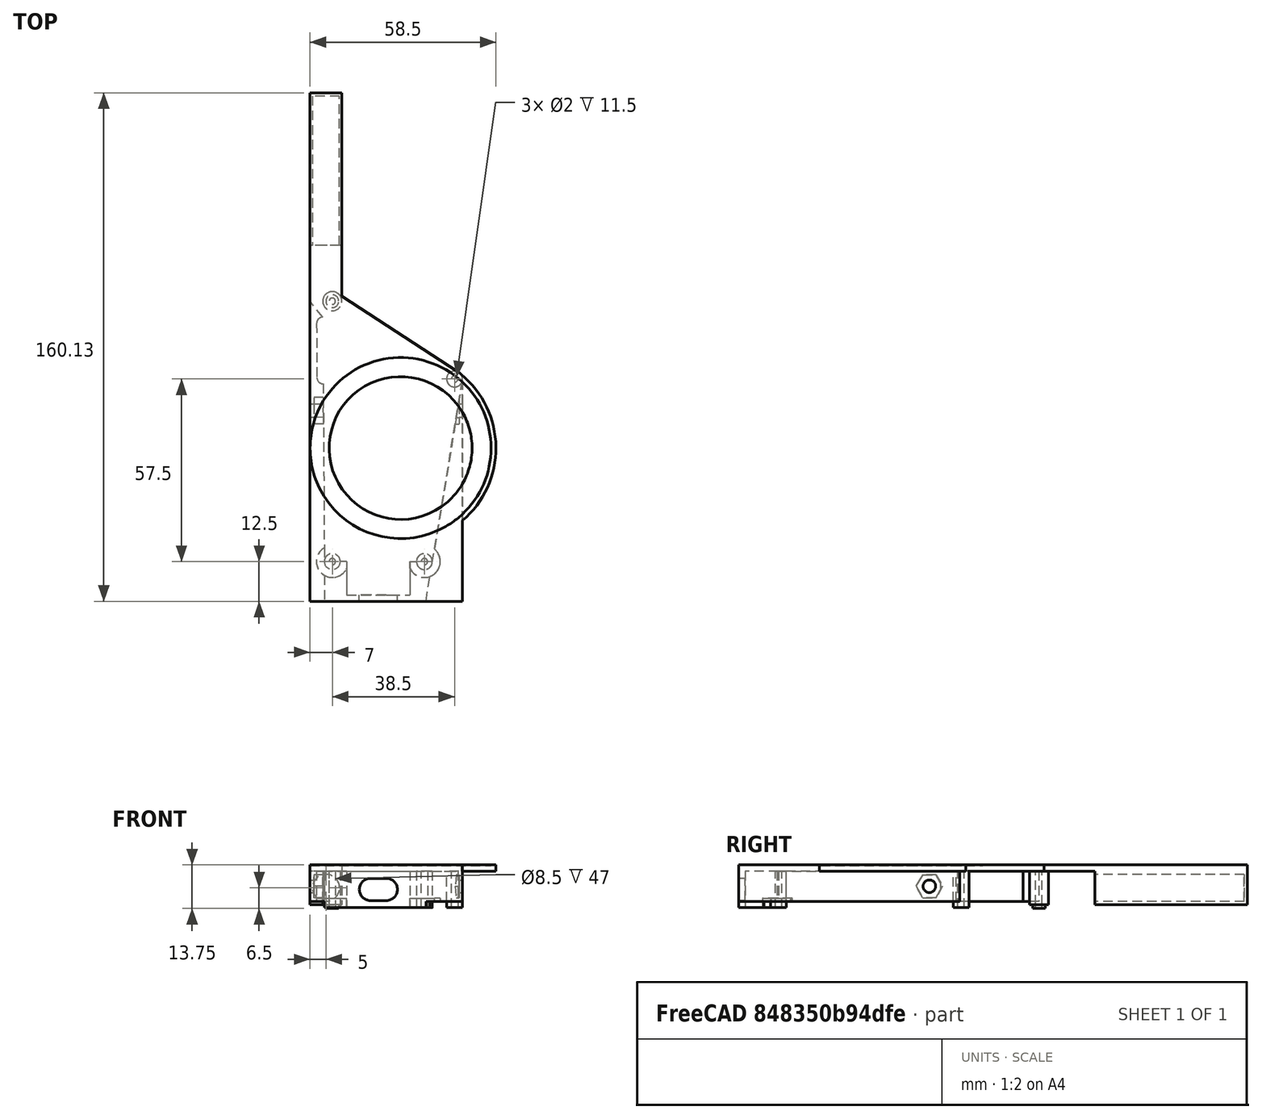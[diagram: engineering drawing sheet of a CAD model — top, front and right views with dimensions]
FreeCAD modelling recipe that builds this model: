
FCSTD DOCUMENT  (FreeCAD 0.19R24276 (Git))
Label: dims_test
License: All rights reserved
LicenseURL: http://en.wikipedia.org/wiki/All_rights_reserved
objects: Sketcher::SketchObject×17, PartDesign::Pad×9, PartDesign::Pocket×8, Spreadsheet::Sheet×2, PartDesign::Plane×1, PartDesign::Body×1, Part::Mirroring×1
note: 54 computed .brp shape members not serialized (recipe doc carries the construction recipe); baked Part::Feature solids carry a one-line shape summary decoded from their .brp

FEATURE [Spreadsheet::Sheet] Spreadsheet  label="dims"
  cells = A1=bottom screw gap; B1(bottom_screw_gap)=29; A2=bottom to antenna; B2(bottom_to_antenna_gap)=82; A3=standoff height; B3(standoff_height)=11.5; A4=standoff diam; B4(standoff_diam)=5; A5=antenna snugger diam; B5(antenna_snugger_diam)=4; A6=antenna snugger height; B6(antenna_snugger_height)=1.25; A7=standoff screw diam; B7(screw_diam)=2; A8=antenna standoff width; B8(antenna_standoff_diam)=6; A9=antenna standoff height; B9(antenna_standoff_height)==standoff_height - 1; A10=side mount offset height; B10(side_mount_offset_height)=57.5; A11=side mount offset width; B11(side_mount_offset_width)=9.5; A13=antenna diam; B13(antenna_diam)=8.5; A15=ring outer diam; B15(ring_outer_diam)==57mm; A16=ring inner diam; B16(ring_inner_diam)==45mm; A17=ring thickness; B17(ring_thickness)==0.25mm
FEATURE [Sketcher::SketchObject] Sketch
  FullyConstrained = true
  MapMode = 5
  Support = -> [XY_Plane]
  expr: Constraints[13] = <<dims>>.bottom_screw_gap
  expr: Constraints[12] = <<dims>>.standoff_diam
  expr: Constraints[3] = <<dims>>.screw_diam
  expr: Constraints[4] = <<dims>>.bottom_to_antenna_gap
  expr: Constraints[25] = <<dims>>.antenna_standoff_diam
  expr: Constraints[18] = <<dims>>.side_mount_offset_width
  expr: Constraints[17] = <<dims>>.side_mount_offset_height
  expr: Constraints[47] = <<otg_adapter_dims>>.stickout
  sketch-geometry (18):
    g0: Circle CenterX=0 CenterY=0 CenterZ=0 NormalX=0 NormalY=0 NormalZ=1 AngleXU=0 Radius=1
    g1: Circle CenterX=0 CenterY=82 CenterZ=0 NormalX=0 NormalY=0 NormalZ=1 AngleXU=0 Radius=1
    g2: Circle CenterX=0 CenterY=82 CenterZ=0 NormalX=0 NormalY=0 NormalZ=1 AngleXU=0 Radius=2.5
    g3: Circle CenterX=0 CenterY=0 CenterZ=0 NormalX=0 NormalY=0 NormalZ=1 AngleXU=0 Radius=2.5
    g4: Circle CenterX=29 CenterY=0 CenterZ=0 NormalX=0 NormalY=0 NormalZ=1 AngleXU=0 Radius=2.5
    g5: Circle CenterX=29 CenterY=0 CenterZ=0 NormalX=0 NormalY=0 NormalZ=1 AngleXU=0 Radius=2.5
    g6: Circle CenterX=38.5 CenterY=57.5 CenterZ=0 NormalX=0 NormalY=0 NormalZ=1 AngleXU=0 Radius=2.5
    g7: Circle CenterX=38.5 CenterY=57.5 CenterZ=0 NormalX=0 NormalY=0 NormalZ=1 AngleXU=0 Radius=1
    g8: Circle CenterX=29 CenterY=0 CenterZ=0 NormalX=0 NormalY=0 NormalZ=1 AngleXU=0 Radius=1
    g9: LineSegment StartX=1.63826 StartY=84.5132 StartZ=0 EndX=39.8652 EndY=59.5943 EndZ=0
    g10: LineSegment StartX=31.4666 StartY=-0.4075 StartZ=0 EndX=40.9666 EndY=57.0925 EndZ=0
    g11: Circle CenterX=0 CenterY=82 CenterZ=0 NormalX=0 NormalY=0 NormalZ=1 AngleXU=0 Radius=3
    g12: ArcOfCircle CenterX=0 CenterY=82 CenterZ=0 NormalX=0 NormalY=0 NormalZ=1 AngleXU=0 Radius=3 StartAngle=0.99311 EndAngle=3.14769
    g13: ArcOfCircle CenterX=38.5 CenterY=57.5 CenterZ=0 NormalX=0 NormalY=0 NormalZ=1 AngleXU=0 Radius=2.5 StartAngle=6.11945 EndAngle=7.27629
    g14: LineSegment StartX=31.4666 StartY=-0.4075 StartZ=0 EndX=29.4687 EndY=-12.5 EndZ=0
    g15: LineSegment StartX=-2.42383 StartY=-12.5 StartZ=0 EndX=29.4687 EndY=-12.5 EndZ=0
    g16: LineSegment StartX=-2.99994 StartY=81.9817 StartZ=0 EndX=-2.42383 EndY=-12.5 EndZ=0
    g17: LineSegment StartX=-2.4848 StartY=-2.5 StartZ=0 EndX=31.1208 EndY=-2.5 EndZ=0
  constraints (48):
    c: Coincident(g0,g-1)
    c: PointOnObject(g1,g-2)
    c: Equal(g1,g0)
    c: Diameter(g1) = 2
    c: Distance(g1,g0) = 82
    c: Coincident(g2,g1)
    c: Coincident(g3,g0)
    c: PointOnObject(g4,g-1)
    c: Equal(g3,g4)
    c: Coincident(g5,g4)
    c: Equal(g3,g5)
    c: Equal(g5,g2)
    c: Diameter(g2) = 5
    c: Distance(g4,g0) = 29
    c: Coincident(g7,g6)
    c: Equal(g1,g7)
    c: Equal(g6,g2)
    c: DistanceY(g4,g6) = 57.5
    c: DistanceX(g4,g6) = 9.5
    c: Coincident(g8,g4)
    c: Equal(g0,g8)
    c: Tangent(g9,g6)
    c: Tangent(g10,g4)
    c: Tangent(g10,g6)
    c: Coincident(g11,g1)
    c: Diameter(g11) = 6
    c: Tangent(g9,g11)
    c: PointOnObject(g9,g11)
    c: Coincident(g12,g1)
    c: Coincident(g12,g9)
    c: Coincident(g9,g13)
    c: Coincident(g10,g13)
    c: PointOnObject(g10,g6)
    c: PointOnObject(g10,g4)
    c: Coincident(g13,g6)
    c: Coincident(g14,g10)
    c: Coincident(g15,g14)
    c: Horizontal(g15)
    c: Parallel(g14,g10)
    c: Coincident(g16,g12)
    c: Coincident(g16,g15)
    c: Tangent(g16,g3)
    c: Tangent(g16,g11)
    c: PointOnObject(g17,g16)
    c: PointOnObject(g17,g14)
    c: Horizontal(g17)
    c: Tangent(g17,g4)
    c: DistanceY(g14,g17) = 10
FEATURE [PartDesign::Pad] Pad  label="base plate"
  Direction = (1,1,1)
  Length = 2
  Length2 = 100
  Profile = -> Sketch
  Type = 0
FEATURE [Sketcher::SketchObject] Sketch001
  ExternalGeometry = -> [Pad]
  FullyConstrained = true
  MapMode = 5
  Placement = pos=(0,0,2) rot=(0,0,1;0rad)
  Support = -> [Pad]
  expr: Constraints[4] = <<dims>>.screw_diam
  expr: Constraints[10] = <<dims>>.bottom_screw_gap
  expr: Constraints[12] = <<dims>>.standoff_diam
  sketch-geometry (6):
    g0: Circle CenterX=0 CenterY=0 CenterZ=0 NormalX=0 NormalY=0 NormalZ=1 AngleXU=0 Radius=2.5
    g1: Circle CenterX=29 CenterY=0 CenterZ=0 NormalX=0 NormalY=0 NormalZ=1 AngleXU=0 Radius=2.5
    g2: Circle CenterX=29 CenterY=0 CenterZ=0 NormalX=0 NormalY=0 NormalZ=1 AngleXU=0 Radius=1
    g3: Circle CenterX=0 CenterY=0 CenterZ=0 NormalX=0 NormalY=0 NormalZ=1 AngleXU=0 Radius=1
    g4: Circle CenterX=38.5 CenterY=57.5 CenterZ=0 NormalX=0 NormalY=0 NormalZ=1 AngleXU=0 Radius=2.5
    g5: Circle CenterX=38.5 CenterY=57.5 CenterZ=0 NormalX=0 NormalY=0 NormalZ=1 AngleXU=0 Radius=1
  constraints (13):
    c: Coincident(g0,g-1)
    c: Coincident(g2,g1)
    c: Coincident(g3,g0)
    c: Equal(g2,g3)
    c: Diameter(g3) = 2
    c: Equal(g0,g1)
    c: Coincident(g4,g-4)
    c: Coincident(g5,g4)
    c: Equal(g3,g5)
    c: PointOnObject(g1,g-1)
    c: DistanceX(g0,g1) = 29
    c: Equal(g4,g1)
    c: Diameter(g1) = 5
FEATURE [PartDesign::Pad] Pad003  label="standoffs"
  BaseFeature = -> Pad
  Direction = (1,1,1)
  Length = 11.5
  Length2 = 100
  Profile = -> Sketch001
  Type = 0
  expr: Length = <<dims>>.standoff_height
FEATURE [Sketcher::SketchObject] Sketch003
  ExternalGeometry = -> [Pad003]
  FullyConstrained = true
  MapMode = 5
  Placement = pos=(0,0,2) rot=(0,0,1;0rad)
  Support = -> [Pad003]
  expr: Constraints[3] = <<dims>>.screw_diam
  sketch-geometry (2):
    g0: Circle CenterX=0 CenterY=82 CenterZ=0 NormalX=0 NormalY=0 NormalZ=1 AngleXU=0 Radius=3
    g1: Circle CenterX=0 CenterY=82 CenterZ=0 NormalX=0 NormalY=0 NormalZ=1 AngleXU=0 Radius=1
  constraints (4):
    c: Coincident(g0,g-3)
    c: PointOnObject(g-3,g0)
    c: Coincident(g1,g0)
    c: Diameter(g1) = 2
FEATURE [PartDesign::Pad] Pad004  label="antenna standoff"
  BaseFeature = -> Pad003
  Direction = (1,1,1)
  Length = 10.5
  Length2 = 100
  Profile = -> Sketch003
  Type = 0
  expr: Length = <<dims>>.antenna_standoff_height
FEATURE [Sketcher::SketchObject] Sketch006
  ExternalGeometry = -> [Pad004]
  FullyConstrained = true
  MapMode = 5
  Placement = pos=(0,0,12.5) rot=(0,0,1;0rad)
  Support = -> [Pad004]
  expr: Constraints[3] = <<dims>>.antenna_snugger_diam
  sketch-geometry (2):
    g0: Circle CenterX=0 CenterY=82 CenterZ=0 NormalX=0 NormalY=0 NormalZ=1 AngleXU=0 Radius=2
    g1: Circle CenterX=0 CenterY=82 CenterZ=0 NormalX=0 NormalY=0 NormalZ=1 AngleXU=0 Radius=1
  constraints (4):
    c: Coincident(g0,g-3)
    c: Coincident(g1,g0)
    c: Equal(g1,g-3)
    c: Diameter(g0) = 4
FEATURE [PartDesign::Pad] Pad007  label="antenna snugger"
  BaseFeature = -> Pad004
  Direction = (1,1,1)
  Length = 1.25
  Length2 = 100
  Profile = -> Sketch006
  Type = 0
  expr: Length = <<dims>>.antenna_snugger_height
FEATURE [Spreadsheet::Sheet] Spreadsheet001  label="otg_adapter_dims"
  cells = A1=width; B1(width)=20; A2=length; B2(length)=32; A3=lightning width; B3(lightning_width)=12; A4=lightning height; B4(lightning_height)=7; A5=stickout; B5(stickout)=10
FEATURE [Sketcher::SketchObject] Sketch011
  ExternalGeometry = -> [Pad007]
  FullyConstrained = true
  MapMode = 5
  Support = -> [XY_Plane]
  sketch-geometry (8):
    g0: LineSegment StartX=-7 StartY=147.626 StartZ=0 EndX=3 EndY=147.626 EndZ=0
    g1: LineSegment StartX=3 StartY=147.626 StartZ=0 EndX=3 EndY=83.6255 EndZ=0
    g2: LineSegment StartX=-7 StartY=147.626 StartZ=0 EndX=-7 EndY=82 EndZ=0
    g3: LineSegment StartX=-7 StartY=82 StartZ=0 EndX=-2.96946 EndY=76.9817 EndZ=0
    g4: LineSegment StartX=1.63826 StartY=84.5132 StartZ=0 EndX=3 EndY=83.6255 EndZ=0
    g5: ArcOfCircle CenterX=0 CenterY=82 CenterZ=0 NormalX=0 NormalY=0 NormalZ=1 AngleXU=0 Radius=3 StartAngle=0.99311 EndAngle=3.14769
    g6: LineSegment StartX=-7 StartY=82 StartZ=0 EndX=3 EndY=82 EndZ=0
    g7: LineSegment StartX=-2.99994 StartY=81.9817 StartZ=0 EndX=-2.96946 EndY=76.9817 EndZ=0
  constraints (23):
    c: Horizontal(g0)
    c: Coincident(g1,g0)
    c: PointOnObject(g1,g-3)
    c: Vertical(g1)
    c: Coincident(g2,g0)
    c: Vertical(g2)
    c: Coincident(g3,g2)
    c: PointOnObject(g3,g-5)
    c: Coincident(g4,g-3)
    c: Coincident(g4,g1)
    c: Coincident(g5,g-4)
    c: Coincident(g5,g4)
    c: PointOnObject(g5,g-5)
    c: DistanceY(g3,g5) = 5
    c: Coincident(g6,g2)
    c: PointOnObject(g6,g-4)
    c: Horizontal(g6)
    c: PointOnObject(g5,g6)
    c: Distance(g0) = 10
    c: Tangent(g1,g-4)
    c: Coincident(g7,g5)
    c: Coincident(g7,g3)
    c: Distance(g1) = 64
FEATURE [PartDesign::Pad] Pad010  label="antenna cover base"
  BaseFeature = -> Pad007
  Direction = (1,1,1)
  Length = 10
  Length2 = 100
  Profile = -> Sketch011
  Type = 3
  UpToFace = -> Pad007 [Face7]
FEATURE [Sketcher::SketchObject] Sketch008
  ExternalGeometry = -> [Pad010]
  FullyConstrained = true
  MapMode = 5
  Placement = pos=(0,0,2) rot=(0,0,1;0rad)
  Support = -> [Pad010]
  sketch-geometry (4):
    g0: LineSegment StartX=-7 StartY=147.626 StartZ=0 EndX=3 EndY=147.626 EndZ=0
    g1: LineSegment StartX=3 StartY=147.626 StartZ=0 EndX=3 EndY=99.6255 EndZ=0
    g2: LineSegment StartX=3 StartY=99.6255 StartZ=0 EndX=-7 EndY=99.6255 EndZ=0
    g3: LineSegment StartX=-7 StartY=99.6255 StartZ=0 EndX=-7 EndY=147.626 EndZ=0
  constraints (11):
    c: Coincident(g0,g1)
    c: Coincident(g1,g2)
    c: Coincident(g2,g3)
    c: Coincident(g3,g0)
    c: Horizontal(g0)
    c: Horizontal(g2)
    c: Vertical(g1)
    c: Vertical(g3)
    c: Coincident(g0,g-5)
    c: PointOnObject(g1,g-4)
    c: Distance(g1) = 48
FEATURE [PartDesign::Pad] Pad009  label="antenna cover meat"
  BaseFeature = -> Pad010
  Direction = (1,1,1)
  Length = 10.5
  Length2 = 100
  Profile = -> Sketch008
  Type = 0
  expr: Length = <<dims>>.antenna_standoff_height
FEATURE [Sketcher::SketchObject] Sketch009
  ExternalGeometry = -> [Pad009]
  FullyConstrained = true
  MapMode = 5
  Placement = pos=(0,99.6255,0) rot=(1,0,0;1.5708rad)
  Support = -> [Pad009]
  expr: Constraints[10] = <<dims>>.antenna_diam
  sketch-geometry (4):
    g0: Circle CenterX=-2 CenterY=7.25 CenterZ=0 NormalX=0 NormalY=0 NormalZ=1 AngleXU=0 Radius=4.25
    g1: LineSegment StartX=-7 StartY=2 StartZ=0 EndX=3 EndY=2 EndZ=0
    g2: LineSegment StartX=-2 StartY=12.5 StartZ=0 EndX=-2 EndY=2 EndZ=0
    g3: LineSegment StartX=-7 StartY=7.25 StartZ=0 EndX=3 EndY=7.25 EndZ=0
  constraints (11):
    c: Coincident(g1,g-3)
    c: Coincident(g1,g-5)
    c: PointOnObject(g2,g1)
    c: Vertical(g2)
    c: Symmetric(g-4,g-5,g2)
    c: Horizontal(g3)
    c: PointOnObject(g3,g-5)
    c: PointOnObject(g0,g3)
    c: PointOnObject(g0,g2)
    c: Symmetric(g-4,g1,g3)
    c: Diameter(g0) = 8.5
FEATURE [PartDesign::Pocket] Pocket  label="antenna pocket"
  BaseFeature = -> Pad009
  Length = 47
  Length2 = 100
  Profile = -> Sketch009
  Type = 0
  expr: Length = 47
FEATURE [Sketcher::SketchObject] Sketch012
  ExternalGeometry = -> [Pocket]
  FullyConstrained = true
  MapMode = 5
  Placement = pos=(0,0,2) rot=(0,0,1;0rad)
  Support = -> [Pocket]
  expr: Constraints[11] = <<otg_adapter_dims>>.width
  sketch-geometry (12):
    g0: LineSegment StartX=4.5 StartY=3e-16 StartZ=0 EndX=24.5 EndY=3e-16 EndZ=0
    g1: GeomPoint X=14.5 Y=0 Z=0
    g2: LineSegment StartX=4.5 StartY=3e-16 StartZ=0 EndX=2.5 EndY=3e-16 EndZ=0
    g3: LineSegment StartX=-2.42383 StartY=-12.5 StartZ=0 EndX=-2.49995 EndY=-0.0152438 EndZ=0
    g4: ArcOfCircle CenterX=0 CenterY=0 CenterZ=0 NormalX=0 NormalY=0 NormalZ=1 AngleXU=0 Radius=2.5 StartAngle=3.14769 EndAngle=6.28319
    g5: LineSegment StartX=4.5 StartY=3e-16 StartZ=0 EndX=4.5 EndY=-10.5 EndZ=0
    g6: LineSegment StartX=4.5 StartY=-10.5 StartZ=0 EndX=24.5 EndY=-10.5 EndZ=0
    g7: LineSegment StartX=29.4687 StartY=-12.5 StartZ=0 EndX=31.4666 EndY=-0.4075 EndZ=0
    g8: LineSegment StartX=24.5 StartY=3e-16 StartZ=0 EndX=26.5 EndY=3e-16 EndZ=0
    g9: LineSegment StartX=24.5 StartY=3e-16 StartZ=0 EndX=24.5 EndY=-10.5 EndZ=0
    g10: LineSegment StartX=-2.42383 StartY=-12.5 StartZ=0 EndX=29.4687 EndY=-12.5 EndZ=0
    g11: ArcOfCircle CenterX=29 CenterY=0 CenterZ=0 NormalX=0 NormalY=0 NormalZ=1 AngleXU=0 Radius=2.5 StartAngle=3.14159 EndAngle=6.11945
  constraints (28):
    c: Symmetric(g-7,g-1,g1)
    c: Symmetric(g0,g0,g1)
    c: Coincident(g2,g0)
    c: Horizontal(g2)
    c: Horizontal(g0)
    c: Coincident(g3,g-4)
    c: Coincident(g4,g-1)
    c: Coincident(g4,g3)
    c: Coincident(g4,g2)
    c: Coincident(g5,g2)
    c: Vertical(g5)
    c: Distance(g2,g0) = 20
    c: Coincident(g6,g5)
    c: Horizontal(g6)
    c: Coincident(g7,g-5)
    c: Coincident(g8,g0)
    c: Horizontal(g8)
    c: Coincident(g9,g8)
    c: Coincident(g9,g6)
    c: Vertical(g9)
    c: DistanceY(g7,g6) = 2
    c: Coincident(g7,g-5)
    c: Coincident(g-4,g3)
    c: Coincident(g10,g3)
    c: Coincident(g10,g7)
    c: Coincident(g11,g-7)
    c: Coincident(g11,g8)
    c: Coincident(g11,g7)
FEATURE [PartDesign::Pad] Pad011  label="otg adapter holder"
  BaseFeature = -> Pocket
  Direction = (1,1,1)
  Length = 11.5
  Length2 = 100
  Profile = -> Sketch012
  Type = 0
  expr: Length = <<dims>>.standoff_height
FEATURE [Sketcher::SketchObject] Sketch013
  ExternalGeometry = -> [Pad011]
  FullyConstrained = true
  MapMode = 5
  Placement = pos=(0,-10.5,0) rot=(0,0.707107,0.707107;3.14159rad)
  Support = -> [Pad011]
  expr: Constraints[6] = <<otg_adapter_dims>>.lightning_height
  expr: Constraints[7] = <<otg_adapter_dims>>.lightning_width - <<otg_adapter_dims>>.lightning_height
  sketch-geometry (11):
    g0: ArcOfCircle CenterX=-17 CenterY=7.75 CenterZ=0 NormalX=0 NormalY=0 NormalZ=1 AngleXU=0 Radius=3.5 StartAngle=1.5708 EndAngle=4.71239
    g1: ArcOfCircle CenterX=-12 CenterY=7.75 CenterZ=0 NormalX=0 NormalY=0 NormalZ=1 AngleXU=0 Radius=3.5 StartAngle=4.71239 EndAngle=7.85398
    g2: LineSegment StartX=-17 StartY=4.25 StartZ=0 EndX=-12 EndY=4.25 EndZ=0
    g3: LineSegment StartX=-17 StartY=11.25 StartZ=0 EndX=-12 EndY=11.25 EndZ=0
    g4: LineSegment StartX=-20.5 StartY=11.25 StartZ=0 EndX=-8.5 EndY=11.25 EndZ=0
    g5: LineSegment StartX=-8.5 StartY=11.25 StartZ=0 EndX=-8.5 EndY=4.25 EndZ=0
    g6: LineSegment StartX=-8.5 StartY=4.25 StartZ=0 EndX=-20.5 EndY=4.25 EndZ=0
    g7: LineSegment StartX=-20.5 StartY=4.25 StartZ=0 EndX=-20.5 EndY=11.25 EndZ=0
    g8: LineSegment StartX=-14.5 StartY=13.5 StartZ=0 EndX=-14.5 EndY=2 EndZ=0
    g9: GeomPoint X=-14.5 Y=4.25 Z=0
    g10: LineSegment StartX=-24.5 StartY=7.75 StartZ=0 EndX=-4.5 EndY=7.75 EndZ=0
  constraints (29):
    c: Tangent(g0,g3) = 1.5708
    c: Tangent(g0,g2) = -1.5708
    c: Tangent(g2,g1) = -1.5708
    c: Tangent(g3,g1) = 1.5708
    c: Horizontal(g2)
    c: Equal(g0,g1)
    c: Distance(g0,g0) = 7
    c: Distance(g3) = 5
    c: Coincident(g4,g5)
    c: Coincident(g5,g6)
    c: Coincident(g6,g7)
    c: Coincident(g7,g4)
    c: Horizontal(g4)
    c: Horizontal(g6)
    c: Vertical(g5)
    c: Vertical(g7)
    c: PointOnObject(g1,g6)
    c: PointOnObject(g1,g4)
    c: Tangent(g5,g1)
    c: Tangent(g7,g0)
    c: PointOnObject(g8,g-5)
    c: Vertical(g8)
    c: Symmetric(g-6,g-6,g8)
    c: Symmetric(g0,g1,g9)
    c: PointOnObject(g9,g8)
    c: PointOnObject(g10,g-4)
    c: Horizontal(g10)
    c: Symmetric(g-5,g-6,g10)
    c: PointOnObject(g0,g10)
FEATURE [PartDesign::Pocket] Pocket001  label="lightning pocket"
  BaseFeature = -> Pad011
  Length = 5
  Length2 = 100
  Profile = -> Sketch013
  Type = 2
FEATURE [Sketcher::SketchObject] Sketch014
  ExternalGeometry = -> [Pocket001]
  FullyConstrained = true
  MapMode = 5
  Support = -> [XY_Plane]
  sketch-geometry (7):
    g0: LineSegment StartX=-7 StartY=82 StartZ=0 EndX=-2.96946 EndY=76.9817 EndZ=0
    g1: LineSegment StartX=-7 StartY=82 StartZ=0 EndX=-7 EndY=-12.5 EndZ=0
    g2: LineSegment StartX=-7 StartY=-12.5 StartZ=0 EndX=-2.42383 EndY=-12.5 EndZ=0
    g3: LineSegment StartX=-2.96946 StartY=76.9817 StartZ=0 EndX=-2.42383 EndY=-12.5 EndZ=0
    g4: LineSegment StartX=40.9666 StartY=57.0925 StartZ=0 EndX=29.4687 EndY=-12.5 EndZ=0
    g5: LineSegment StartX=40.9666 StartY=57.0925 StartZ=0 EndX=40.9666 EndY=-12.5 EndZ=0
    g6: LineSegment StartX=29.4687 StartY=-12.5 StartZ=0 EndX=40.9666 EndY=-12.5 EndZ=0
  constraints (16):
    c: Coincident(g0,g-3)
    c: Coincident(g0,g-4)
    c: Coincident(g1,g0)
    c: Vertical(g1)
    c: Coincident(g2,g1)
    c: Coincident(g2,g-5)
    c: Horizontal(g2)
    c: Coincident(g3,g0)
    c: Coincident(g3,g2)
    c: Coincident(g4,g-6)
    c: Coincident(g4,g-5)
    c: Coincident(g5,g4)
    c: Coincident(g6,g4)
    c: Coincident(g6,g5)
    c: Horizontal(g6)
    c: Vertical(g5)
FEATURE [PartDesign::Pad] Pad012
  BaseFeature = -> Pocket001
  Direction = (1,1,1)
  Length = 11.5
  Length2 = 100
  Profile = -> Sketch014
  Type = 0
  expr: Length = <<dims>>.standoff_height
FEATURE [PartDesign::Plane] DatumPlane
  AttachmentOffset = pos=(0,0,-3) rot=(0,0,1;0rad)
  Length = 191.206
  MapMode = 5
  Placement = pos=(37.9666,0,0) rot=(0.57735,0.57735,0.57735;2.0944rad)
  ResizeMode = 0
  Support = -> [Pad012]
  Width = 68.5809
FEATURE [Sketcher::SketchObject] Sketch016
  ExternalGeometry = -> [Pad012]
  FullyConstrained = true
  MapMode = 5
  Placement = pos=(37.9666,0,0) rot=(0.57735,0.57735,0.57735;2.0944rad)
  Support = -> [DatumPlane]
  sketch-geometry (9):
    g0: LineSegment StartX=51.6569 StartY=6.75 StartZ=0 EndX=49.5785 EndY=10.35 EndZ=0
    g1: LineSegment StartX=49.5785 StartY=10.35 StartZ=0 EndX=45.4215 EndY=10.35 EndZ=0
    g2: LineSegment StartX=45.4215 StartY=10.35 StartZ=0 EndX=43.3431 EndY=6.75 EndZ=0
    g3: LineSegment StartX=43.3431 StartY=6.75 StartZ=0 EndX=45.4215 EndY=3.15 EndZ=0
    g4: LineSegment StartX=45.4215 StartY=3.15 StartZ=0 EndX=49.5785 EndY=3.15 EndZ=0
    g5: LineSegment StartX=49.5785 StartY=3.15 StartZ=0 EndX=51.6569 EndY=6.75 EndZ=0
    g6: Circle CenterX=47.5 CenterY=6.75 CenterZ=0 NormalX=0 NormalY=0 NormalZ=1 AngleXU=0 Radius=4.15692
    g7: LineSegment StartX=-12.5 StartY=11.5 StartZ=0 EndX=47.5 EndY=11.5 EndZ=0
    g8: LineSegment StartX=47.5 StartY=11.5 StartZ=0 EndX=47.5 EndY=2 EndZ=0
  constraints (22):
    c: Coincident(g0,g1)
    c: Coincident(g1,g2)
    c: Coincident(g2,g3)
    c: Coincident(g3,g4)
    c: Coincident(g4,g5)
    c: Coincident(g5,g0)
    c: Equal(g0, g1-g5) x5
    c: PointOnObject(g0,g6)
    c: PointOnObject(g1,g6)
    c: PointOnObject(g2,g6)
    c: PointOnObject(g3,g6)
    c: PointOnObject(g4,g6)
    c: PointOnObject(g5,g6)
    c: Horizontal(g4)
    c: Distance(g3,g0) = 7.2
    c: Coincident(g7,g-3)
    c: Horizontal(g7)
    c: Distance(g7) = 60
    c: Coincident(g8,g7)
    c: PointOnObject(g8,g-4)
    c: Vertical(g8)
    c: Symmetric(g8,g7,g6)
FEATURE [PartDesign::Pocket] Pocket002
  BaseFeature = -> Pad012
  Length = 2
  Length2 = 100
  Profile = -> Sketch016
  Reversed = true
  Type = 0
FEATURE [Sketcher::SketchObject] Sketch017
  ExternalGeometry = -> [Pocket002]
  FullyConstrained = true
  MapMode = 5
  Placement = pos=(37.9666,0,0) rot=(0.57735,0.57735,0.57735;2.0944rad)
  Support = -> [DatumPlane]
  sketch-geometry (2):
    g0: Circle CenterX=47.5 CenterY=6.75 CenterZ=0 NormalX=0 NormalY=0 NormalZ=1 AngleXU=0 Radius=2
    g1: LineSegment StartX=47.5 StartY=11.5 StartZ=0 EndX=47.5 EndY=2 EndZ=0
  constraints (6):
    c: DistanceX(g-5,g0) = 60
    c: PointOnObject(g1,g-3)
    c: Vertical(g1)
    c: Symmetric(g1,g1,g0)
    c: Diameter(g0) = 4
    c: PointOnObject(g1,g-4)
FEATURE [PartDesign::Pocket] Pocket003
  BaseFeature = -> Pocket002
  Length = 100
  Length2 = 100
  Profile = -> Sketch017
  Type = 4
FEATURE [Sketcher::SketchObject] Sketch018
  ExternalGeometry = -> [Pocket003]
  FullyConstrained = false
  MapMode = 5
  Placement = pos=(-2.49995,-0.0152439,0) rot=(0.575003,0.57852,0.57852;2.09792rad)
  Support = -> [Pocket003]
  sketch-geometry (7):
    g0: LineSegment StartX=51.673 StartY=6.75 StartZ=0 EndX=49.5946 EndY=10.35 EndZ=0
    g1: LineSegment StartX=49.5946 StartY=10.35 StartZ=0 EndX=45.4377 EndY=10.35 EndZ=0
    g2: LineSegment StartX=45.4377 StartY=10.35 StartZ=0 EndX=43.3592 EndY=6.75 EndZ=0
    g3: LineSegment StartX=43.3592 StartY=6.75 StartZ=0 EndX=45.4377 EndY=3.15 EndZ=0
    g4: LineSegment StartX=45.4377 StartY=3.15 StartZ=0 EndX=49.5946 EndY=3.15 EndZ=0
    g5: LineSegment StartX=49.5946 StartY=3.15 StartZ=0 EndX=51.673 EndY=6.75 EndZ=0
    g6: Circle CenterX=47.5161 CenterY=6.75 CenterZ=0 NormalX=0 NormalY=0 NormalZ=1 AngleXU=0 Radius=4.15692
  constraints (15):
    c: Coincident(g0,g1)
    c: Coincident(g1,g2)
    c: Coincident(g2,g3)
    c: Coincident(g3,g4)
    c: Coincident(g4,g5)
    c: Coincident(g5,g0)
    c: Equal(g0, g1-g5) x5
    c: PointOnObject(g0,g6)
    c: PointOnObject(g1,g6)
    c: PointOnObject(g2,g6)
    c: PointOnObject(g3,g6)
    c: PointOnObject(g4,g6)
    c: PointOnObject(g5,g6)
    c: Horizontal(g4)
    c: Distance(g3,g0) = 7.2
FEATURE [PartDesign::Pocket] Pocket004
  BaseFeature = -> Pocket003
  Length = 3
  Length2 = 100
  Profile = -> Sketch018
  Type = 0
FEATURE [Sketcher::SketchObject] Sketch019
  ExternalGeometry = -> [Pocket004]
  FullyConstrained = true
  MapMode = 5
  Placement = pos=(0,0,13.5) rot=(0,0,1;0rad)
  Support = -> [Pocket004]
  sketch-geometry (12):
    g0: ArcOfCircle CenterX=0 CenterY=0 CenterZ=0 NormalX=0 NormalY=0 NormalZ=1 AngleXU=0 Radius=2.5 StartAngle=3.14769 EndAngle=6.28319
    g1: Circle CenterX=0 CenterY=0 CenterZ=0 NormalX=0 NormalY=0 NormalZ=1 AngleXU=0 Radius=5
    g2: ArcOfCircle CenterX=0 CenterY=0 CenterZ=0 NormalX=0 NormalY=0 NormalZ=1 AngleXU=0 Radius=5 StartAngle=2.10049 EndAngle=5.83216
    g3: LineSegment StartX=-2.52636 StartY=4.3148 StartZ=0 EndX=-2.49995 EndY=-0.0152438 EndZ=0
    g4: LineSegment StartX=2.5 StartY=-6e-16 StartZ=0 EndX=4.5 EndY=0 EndZ=0
    g5: LineSegment StartX=4.5 StartY=0 StartZ=0 EndX=4.5 EndY=-2.17945 EndZ=0
    g6: Circle CenterX=29 CenterY=0 CenterZ=0 NormalX=0 NormalY=0 NormalZ=1 AngleXU=0 Radius=5
    g7: ArcOfCircle CenterX=29 CenterY=0 CenterZ=0 NormalX=0 NormalY=0 NormalZ=1 AngleXU=0 Radius=5 StartAngle=3.59262 EndAngle=7.16664
    g8: LineSegment StartX=24.5 StartY=-2.17945 StartZ=0 EndX=24.5 EndY=0 EndZ=0
    g9: LineSegment StartX=24.5 StartY=0 StartZ=0 EndX=26.5 EndY=3e-16 EndZ=0
    g10: LineSegment StartX=31.4666 StartY=-0.407494 StartZ=0 EndX=32.1724 EndY=3.86469 EndZ=0
    g11: ArcOfCircle CenterX=29 CenterY=0 CenterZ=0 NormalX=0 NormalY=0 NormalZ=1 AngleXU=0 Radius=2.5 StartAngle=3.14159 EndAngle=6.11946
  constraints (30):
    c: Coincident(g0,g-1)
    c: Coincident(g0,g-4)
    c: Coincident(g1,g0)
    c: Diameter(g1) = 10
    c: Coincident(g2,g0)
    c: PointOnObject(g2,g-8)
    c: PointOnObject(g2,g-10)
    c: PointOnObject(g2,g1)
    c: Coincident(g3,g2)
    c: Coincident(g3,g0)
    c: Coincident(g4,g0)
    c: Coincident(g4,g-8)
    c: Coincident(g5,g4)
    c: Coincident(g5,g2)
    c: Coincident(g6,g-5)
    c: Equal(g6,g1)
    c: Coincident(g7,g6)
    c: PointOnObject(g7,g-12)
    c: PointOnObject(g7,g-9)
    c: PointOnObject(g7,g6)
    c: Coincident(g8,g7)
    c: Coincident(g8,g-9)
    c: Coincident(g9,g8)
    c: Coincident(g9,g-5)
    c: Coincident(g10,g7)
    c: Coincident(g11,g7)
    c: Coincident(g11,g9)
    c: PointOnObject(g0,g-10)
    c: Coincident(g10,g11)
    c: PointOnObject(g10,g-11)
FEATURE [PartDesign::Pocket] Pocket005
  BaseFeature = -> Pocket004
  Length = 3
  Length2 = 100
  Profile = -> Sketch019
  Type = 0
FEATURE [Sketcher::SketchObject] Sketch021
  ExternalGeometry = -> [Pocket005]
  FullyConstrained = true
  MapMode = 5
  Placement = pos=(0,0,11.5) rot=(0,0,1;0rad)
  Support = -> [Pocket005]
  sketch-geometry (8):
    g0: ArcOfCircle CenterX=-2.8536 CenterY=57.9821 CenterZ=0 NormalX=0 NormalY=0 NormalZ=1 AngleXU=0 Radius=2 StartAngle=3.14769 EndAngle=6.28928
    g1: ArcOfCircle CenterX=-2.95726 CenterY=74.9817 CenterZ=0 NormalX=0 NormalY=0 NormalZ=1 AngleXU=0 Radius=2 StartAngle=0.0060976 EndAngle=3.14769
    g2: LineSegment StartX=-0.853639 StartY=57.9943 StartZ=0 EndX=-0.957298 EndY=74.9939 EndZ=0
    g3: LineSegment StartX=-4.85356 StartY=57.9699 StartZ=0 EndX=-4.95722 EndY=74.9695 EndZ=0
    g4: ArcOfCircle CenterX=-2.95726 CenterY=74.9817 CenterZ=0 NormalX=0 NormalY=0 NormalZ=1 AngleXU=0 Radius=2 StartAngle=1.57689 EndAngle=3.14769
    g5: ArcOfCircle CenterX=-2.8536 CenterY=57.9821 CenterZ=0 NormalX=0 NormalY=0 NormalZ=1 AngleXU=0 Radius=2 StartAngle=3.14769 EndAngle=4.71849
    g6: LineSegment StartX=-4.95722 StartY=74.9695 StartZ=0 EndX=-4.85356 EndY=57.9699 EndZ=0
    g7: LineSegment StartX=-2.84141 StartY=55.9821 StartZ=0 EndX=-2.96946 EndY=76.9817 EndZ=0
  constraints (19):
    c: Tangent(g0,g3) = 1.5708
    c: Tangent(g0,g2) = -1.5708
    c: Tangent(g2,g1) = -1.5708
    c: Tangent(g3,g1) = 1.5708
    c: Equal(g0,g1)
    c: PointOnObject(g1,g-5)
    c: PointOnObject(g0,g-5)
    c: Distance(g0,g1) = 17
    c: Distance(g1,g1) = 2
    c: Coincident(g4,g1)
    c: Coincident(g4,g1)
    c: Coincident(g4,g-5)
    c: Coincident(g5,g0)
    c: Coincident(g5,g0)
    c: PointOnObject(g5,g-5)
    c: Coincident(g6,g4)
    c: Coincident(g6,g5)
    c: Coincident(g7,g5)
    c: Coincident(g7,g4)
FEATURE [PartDesign::Pocket] Pocket006
  BaseFeature = -> Pocket005
  Length = 0
  Length2 = 100
  Profile = -> Sketch021
  Type = 3
  UpToFace = -> Pocket005 [Face4]
FEATURE [Sketcher::SketchObject] Sketch022
  ExternalGeometry = -> [Pocket006]
  FullyConstrained = true
  MapMode = 5
  Support = -> [XY_Plane]
  expr: Constraints[5] = <<dims>>.ring_outer_diam + 3mm
  expr: Constraints[2] = <<dims>>.ring_inner_diam
  expr: Constraints[0] = <<dims>>.ring_outer_diam
  sketch-geometry (6):
    g0: Circle CenterX=21.5 CenterY=35.7549 CenterZ=0 NormalX=0 NormalY=0 NormalZ=1 AngleXU=0 Radius=28.5
    g1: Circle CenterX=21.5 CenterY=35.7549 CenterZ=0 NormalX=0 NormalY=0 NormalZ=1 AngleXU=0 Radius=22.5
    g2: Circle CenterX=21.5 CenterY=35.7549 CenterZ=0 NormalX=0 NormalY=0 NormalZ=1 AngleXU=0 Radius=30
    g3: LineSegment StartX=40.9666 StartY=12.9283 StartZ=0 EndX=40.9666 EndY=57.0925 EndZ=0
    g4: ArcOfCircle CenterX=38.5 CenterY=57.5 CenterZ=0 NormalX=0 NormalY=0 NormalZ=1 AngleXU=0 Radius=2.5 StartAngle=6.11945 EndAngle=6.89179
    g5: ArcOfCircle CenterX=21.5 CenterY=35.7549 CenterZ=0 NormalX=0 NormalY=0 NormalZ=1 AngleXU=0 Radius=30 StartAngle=5.41851 EndAngle=7.16592
  constraints (15):
    c: Diameter(g0) = 57
    c: Coincident(g1,g0)
    c: Diameter(g1) = 45
    c: Tangent(g-6,g0)
    c: Coincident(g2,g1)
    c: Diameter(g2) = 60
    c: Tangent(g2,g-3)
    c: PointOnObject(g3,g-5)
    c: Coincident(g3,g-5)
    c: PointOnObject(g3,g2)
    c: Coincident(g4,g-4)
    c: Coincident(g4,g3)
    c: Coincident(g5,g0)
    c: Coincident(g5,g3)
    c: Coincident(g5,g4)
FEATURE [PartDesign::Pad] Pad013
  BaseFeature = -> Pocket006
  Direction = (1,1,1)
  Length = 2
  Length2 = 100
  Profile = -> Sketch022
  Type = 0
FEATURE [Sketcher::SketchObject] Sketch023
  ExternalGeometry = -> [Pad013]
  FullyConstrained = true
  MapMode = 5
  Placement = pos=(0,0,0) rot=(1,0,0;3.14159rad)
  Support = -> [Pad013]
  expr: Constraints[1] = <<dims>>.ring_inner_diam
  expr: Constraints[0] = <<dims>>.ring_outer_diam
  sketch-geometry (2):
    g0: Circle CenterX=21.5 CenterY=-35.7549 CenterZ=0 NormalX=0 NormalY=0 NormalZ=1 AngleXU=0 Radius=28.5
    g1: Circle CenterX=21.5 CenterY=-35.7549 CenterZ=0 NormalX=0 NormalY=0 NormalZ=1 AngleXU=0 Radius=22.5
  constraints (4):
    c: Diameter(g0) = 57
    c: Diameter(g1) = 45
    c: Coincident(g1,g0)
    c: Coincident(g1,g-3)
FEATURE [PartDesign::Pocket] Pocket007
  BaseFeature = -> Pad013
  Length = 0.25
  Length2 = 100
  Profile = -> Sketch023
  Type = 0
  expr: Length = <<dims>>.ring_thickness
FEATURE [PartDesign::Body] Body
  Group = -> [Sketch,Pad,Sketch001,Pad003,Sketch003,Pad004,Sketch006,Pad007,Sketch011,Pad010,Sketch008,Sketch012,Pad009,Sketch009,Pocket,Pad011,Sketch013,Pocket001,Sketch014,Pad012,DatumPlane,Sketch016,Pocket002,Sketch017,Pocket003,Sketch018,Pocket004,Sketch019,Pocket005,Sketch021,Pocket006,Sketch022,Pad013,Sketch023,Pocket007]
  Origin = -> Origin
  Tip = -> Pocket007
FEATURE [Part::Mirroring] Part__Mirroring  label="Body (Mirror #1)"
  Base = (0,0,0)
  Normal = (0,0,1)
  Source = -> Body
